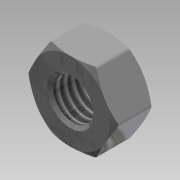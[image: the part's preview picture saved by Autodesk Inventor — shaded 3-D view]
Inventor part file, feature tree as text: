
AUTODESK INVENTOR PART (.ipt)
format: ipt  version: 2014 (Build 180170000, 170)  size: 157,696 bytes
history: native  units: mm
features: sketch x4, extrude x3, hole x1, fillet x1, chamfer x1
ambient origin geometry x8: Origin, YZ Plane, XZ Plane, XY Plane, X Axis, Y Axis, Z Axis, Center Point
bodies: Solid1 (feature_tree)
feature tree (10):
  extrude  "Extrusion1"  Depth=6.5mm TaperAngle=0.0deg
  hole  "Hole1"  [1 undecoded]
  extrude  "Extrusion2"  Depth=0.5mm
  extrude  "Extrusion3"  [1 undecoded]
  fillet  "Fillet1"  [1 undecoded]
  chamfer  "Chamfer1"  [1 undecoded]
  sketch  "Sketch1"  dims[d0=6.5mm d1=6.5mm d2=0.0mm]
  sketch  "Sketch2"  dims[d3=6.647mm d4=6.0mm d5=4.0mm d6=2.0mm d7=90.0deg d8=8.0mm d9=20.594885mm d10=1.0mm d11=-10.471976mm]
  sketch  "Sketch3"  dims[d12=1.0mm d13=-10.471976mm d14=0.5mm]
  sketch  "Sketch4"  dims[d15=0.5mm d16=2.0mm d17=45.0deg]
note: 4 required parameter values undecoded (feature->parameter linkage not recoverable at this tier; creation-order binding heuristic only, values carry confidence <= 0.55)
